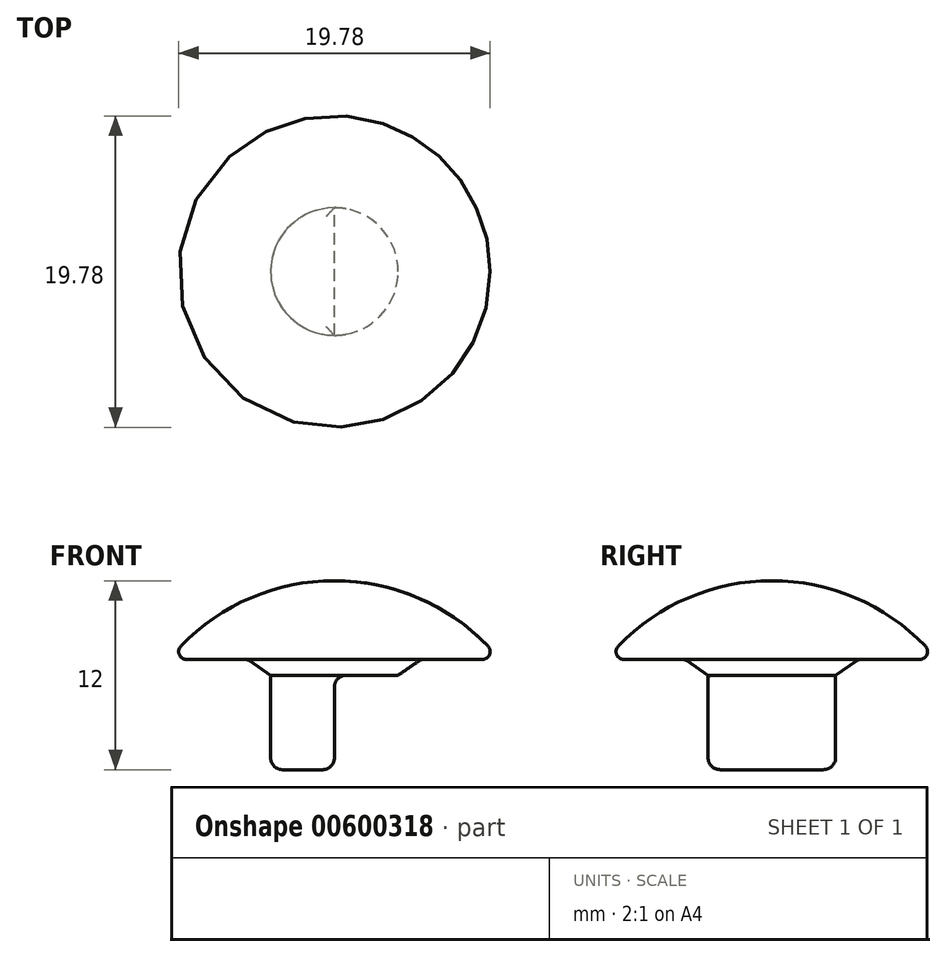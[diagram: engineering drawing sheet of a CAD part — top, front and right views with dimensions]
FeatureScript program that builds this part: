
annotation { "Feature Type Name" : "Feature", "Feature Type Description" : "" }
export const myFeature = defineFeature(function(context is Context, id is Id, definition is map)
    precondition{}
    {
        {
            var Q0;
            Q0=qCreatedBy(makeId("Front.planeOp"),FACE);
            var sketch = newSketch(context, id + "F0", { "sketchPlane" : qUnion([Q0])});
            skLineSegment(sketch, "E0", {"start": v(4.05, 6) * mm, "end": v(5.5, 7) * mm});
            skLineSegment(sketch, "E1", {"start": v(5.5, 7) * mm, "end": v(10.5, 7) * mm});
            skLineSegment(sketch, "E2", {"start": v(0, 12) * mm, "end": v(0, 0) * mm});
            skLineSegment(sketch, "E3", {"start": v(4.05, 6) * mm, "end": v(4.05, 0) * mm});
            skLineSegment(sketch, "E4", {"start": v(4.05, 0) * mm, "end": v(0, 0) * mm});
            skPoint(sketch, "E5.orphan", {"position": v(0, 0) * mm});
            skArc(sketch, "E6", {"start": v(10.5, 7) * mm, "mid": v(5.81, 10.69) * mm, "end": v(0, 12) * mm});
            skSolve(sketch);
        }
        {
            var Q0;
            Q0=qSketchRegion(id+"F0",true);
            var Q1;
            Q1=sQuery(id+"F0.wireOp",EDGE,"E2");
            revolve(context, id + "F1", {"entities" : qUnion([Q0]), "axis" : qUnion([Q1]), "revolveType" : RevolveType.FULL});
        }
        {
            var Q0;
            Q0=makeQuery(id+"F1.opRevolve","SWEPT_FACE",FACE,{"disambiguationData":[OSD([sQuery(id+"F0.wireOp",EDGE,"E4")])]});
            var sketch = newSketch(context, id + "F2", { "sketchPlane" : qUnion([Q0])});
            skLineSegment(sketch, "E7.bottom", {"start": v(0, 4.05) * mm, "end": v(4.05, 4.05) * mm});
            skLineSegment(sketch, "E7.top", {"start": v(0, -4.05) * mm, "end": v(4.05, -4.05) * mm});
            skLineSegment(sketch, "E7.left", {"start": v(0, 4.05) * mm, "end": v(0, -4.05) * mm});
            skLineSegment(sketch, "E7.right", {"start": v(4.05, 4.05) * mm, "end": v(4.05, -4.05) * mm});
            skSolve(sketch);
        }
        {
            var Q0;
            Q0=qSketchRegion(id+"F2",true);
            var Q1;
            Q1=makeQuery(id+"F1.opRevolve","SWEPT_FACE",FACE,{"disambiguationData":[OSD([sQuery(id+"F0.wireOp",EDGE,"36Q2A1E8-CaD5-0Jy8-XmEI-qCisEAcXPKzw")])]});
            extrude(context, id + "F3", {"entities" : qUnion([Q0]), "operationType" : NewBodyOperationType.REMOVE, "oppositeDirection" : true, "depth" : 6 * mm, "endBoundEntityFace" : qUnion([Q1]), "offsetDistance" : 25 * mm});
        }
        {
            var Q0;
            {var subQ2=makeQuery(id+"F2R5GIXbNTLPHZD_2.boolean.opBoolean","COPY",FACE,{"derivedFrom":makeQuery(id+"F2R5GIXbNTLPHZD_2.opExtrude","SWEPT_FACE",FACE,{"disambiguationData":[OSD([sQuery(id+"F2.wireOp",EDGE,"6RF5FfAt-YfcN-XYpJ-voTT-JPPEjn318RsV")])]})});Q0=makeQuery(id+"Fmqv6moUgZnORJw_2.2.F2R5GIXbNTLPHZD_2.boolean.opBoolean","SPLIT",FACE,{"disambiguationData":[TD([subQ2])],"derivedFrom":makeQuery(id+"Fmqv6moUgZnORJw_2.1.F2R5GIXbNTLPHZD_2.boolean.opBoolean","SPLIT",FACE,{"disambiguationData":[TD([subQ2])],"derivedFrom":makeQuery(id+"F1.opRevolve","SWEPT_FACE",FACE,{"disambiguationData":[OSD([sQuery(id+"F0.wireOp",EDGE,"E4")])]})})});}
            var Q1;
            {var subQ1=makeQuery(id+"Fmqv6moUgZnORJw_2.1.F2R5GIXbNTLPHZD_2.opExtrude","SWEPT_FACE",FACE,{"disambiguationData":[OSD([sQuery(id+"F2.wireOp",EDGE,"kqsyaNb8-ErKI-FfWI-nr5y-aiWRytRq8sQ2")])]});var subQ3=sQuery(id+"F2.wireOp",EDGE,"6RF5FfAt-YfcN-XYpJ-voTT-JPPEjn318RsV");Q1=makeQuery(id+"Fmqv6moUgZnORJw_2.2.F2R5GIXbNTLPHZD_2.boolean.opBoolean","SPLIT",FACE,{"disambiguationData":[TD([makeQuery(id+"Fmqv6moUgZnORJw_2.1.F2R5GIXbNTLPHZD_2.boolean.opBoolean","COPY",FACE,{"derivedFrom":subQ1})])],"derivedFrom":makeQuery(id+"Fmqv6moUgZnORJw_2.1.F2R5GIXbNTLPHZD_2.boolean.opBoolean","SPLIT",FACE,{"disambiguationData":[TD([makeQuery(id+"F2R5GIXbNTLPHZD_2.boolean.opBoolean","COPY",FACE,{"derivedFrom":makeQuery(id+"F2R5GIXbNTLPHZD_2.opExtrude","SWEPT_FACE",FACE,{"disambiguationData":[OSD([subQ3])]})})])],"derivedFrom":makeQuery(id+"F1.opRevolve","SWEPT_FACE",FACE,{"disambiguationData":[OSD([sQuery(id+"F0.wireOp",EDGE,"E4")])]})})});}
            var Q2;
            Q2=makeQuery(id+"Fmqv6moUgZnORJw_2.1.F2R5GIXbNTLPHZD_2.boolean.opBoolean","SPLIT",FACE,{"disambiguationData":[TD([makeQuery(id+"F2R5GIXbNTLPHZD_2.boolean.opBoolean","COPY",FACE,{"derivedFrom":makeQuery(id+"F2R5GIXbNTLPHZD_2.opExtrude","SWEPT_FACE",FACE,{"disambiguationData":[OSD([sQuery(id+"F2.wireOp",EDGE,"kqsyaNb8-ErKI-FfWI-nr5y-aiWRytRq8sQ2")])]})})])],"derivedFrom":makeQuery(id+"F1.opRevolve","SWEPT_FACE",FACE,{"disambiguationData":[OSD([sQuery(id+"F0.wireOp",EDGE,"E4")])]})});
            var Q3;
            Q3=makeQuery(id+"F3.boolean.opBoolean","COPY",EDGE,{"derivedFrom":makeQuery(id+"F3.opExtrude","CAP_EDGE",EDGE,{"disambiguationData":[OSD([sQuery(id+"F2.wireOp",EDGE,"E7.left")])],"isStart":false})});
            fillet(context, id + "F4", {"entities" : qUnion([Q0, Q1, Q2, Q3]), "radius" : .75 * mm, "tangentPropagation" : true, "allowEdgeOverflow" : false});
        }
        {
            var Q0;
            Q0=makeQuery(id+"F1.opRevolve","SWEPT_FACE",FACE,{"disambiguationData":[OSD([sQuery(id+"F0.wireOp",EDGE,"E1")])]});
            fillet(context, id + "F5", {"entities" : qUnion([Q0]), "radius" : .5 * mm, "tangentPropagation" : true, "allowEdgeOverflow" : false});
        }
    });
